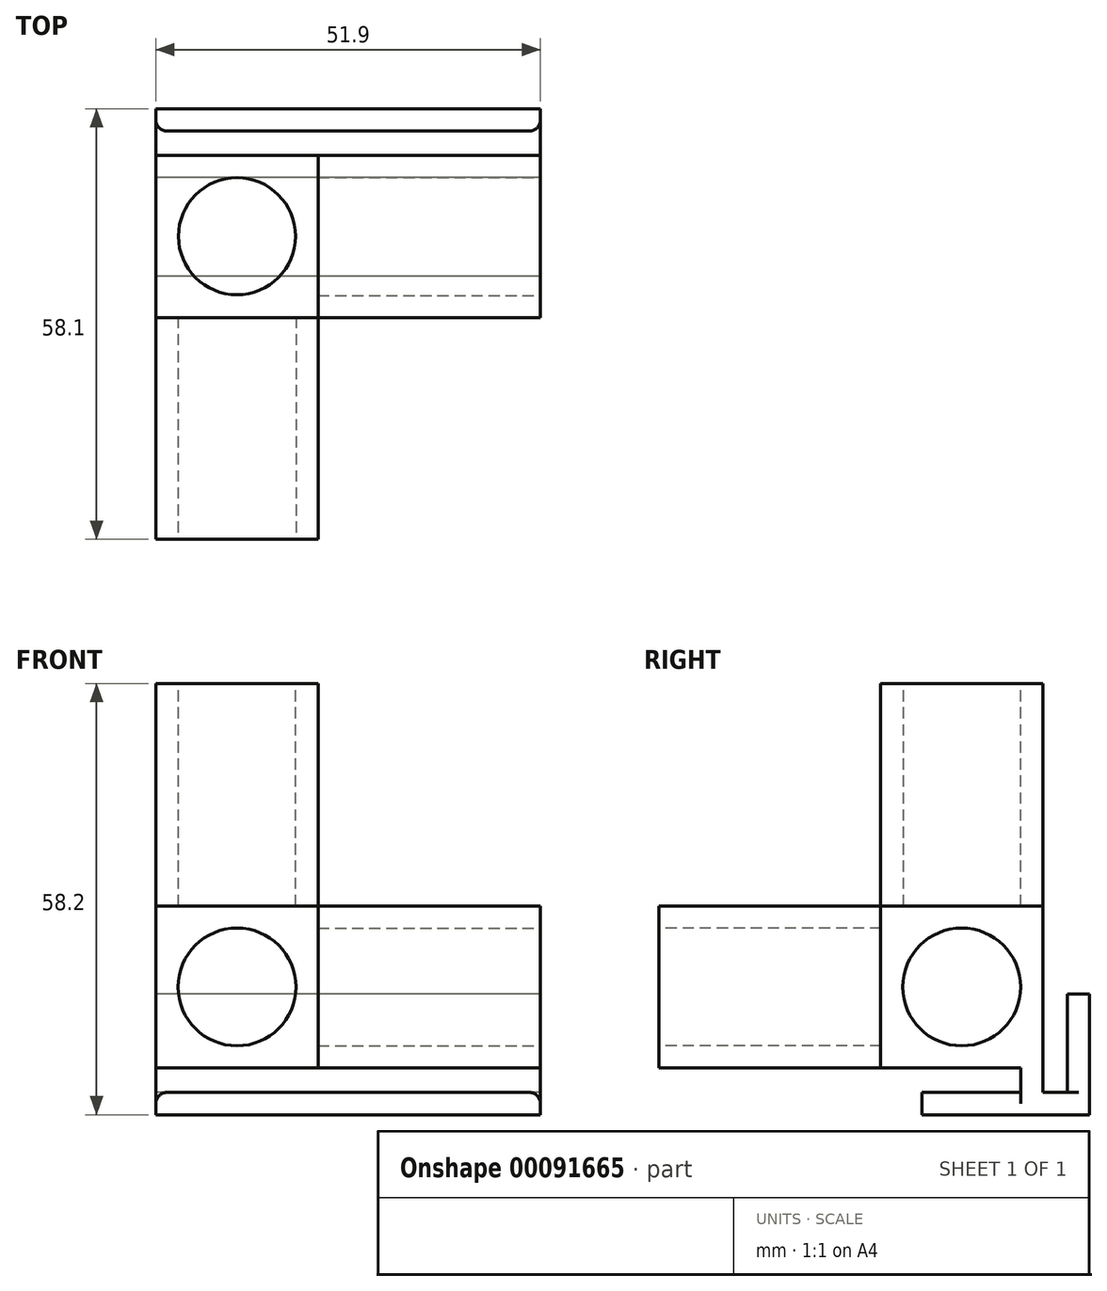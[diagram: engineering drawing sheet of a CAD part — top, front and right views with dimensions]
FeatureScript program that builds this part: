
annotation { "Feature Type Name" : "Feature", "Feature Type Description" : "" }
export const myFeature = defineFeature(function(context is Context, id is Id, definition is map)
    precondition{}
    {
        {
            var Q0;
            Q0=qCreatedBy(makeId("Front.planeOp"),FACE);
            var sketch = newSketch(context, id + "F0", { "sketchPlane" : qUnion([Q0])});
            skLineSegment(sketch, "E0.bottom", {"start": v(-42.3, 45.9) * mm, "end": v(-26.4, 45.9) * mm});
            skLineSegment(sketch, "E0.top", {"start": v(-42.3, 0) * mm, "end": v(-26.4, 0) * mm});
            skLineSegment(sketch, "E0.left", {"start": v(-42.3, 45.9) * mm, "end": v(-42.3, 0) * mm});
            skLineSegment(sketch, "E0.right", {"start": v(-26.4, 45.9) * mm, "end": v(-26.4, 15.9) * mm});
            skLineSegment(sketch, "E1.top", {"start": v(-42.3, 15.9) * mm, "end": v(-26.4, 15.9) * mm});
            skLineSegment(sketch, "E1.left", {"start": v(-42.3, 0) * mm, "end": v(-42.3, 15.9) * mm});
            skLineSegment(sketch, "E1.right", {"start": v(3.6, 0) * mm, "end": v(3.6, 15.9) * mm});
            skLineSegment(sketch, "E2", {"start": v(-26.4, 15.9) * mm, "end": v(-26.4, 0) * mm});
            skLineSegment(sketch, "E3", {"start": v(-26.4, 15.9) * mm, "end": v(3.6, 15.9) * mm});
            skLineSegment(sketch, "E4", {"start": v(-26.4, 0) * mm, "end": v(-26.4, 0) * mm});
            skLineSegment(sketch, "E5", {"start": v(-42.3, 15.9) * mm, "end": v(-42.3, 15.9) * mm});
            skLineSegment(sketch, "E6", {"start": v(-26.4, 0) * mm, "end": v(3.6, 0) * mm});
            skLineSegment(sketch, "E7.0", {"start": v(-45.3, 48.9) * mm, "end": v(-45.3, -3) * mm});
            skLineSegment(sketch, "E7.1", {"start": v(-45.3, -3) * mm, "end": v(-23.4, -3) * mm});
            skLineSegment(sketch, "E7.2", {"start": v(-23.4, 48.9) * mm, "end": v(-23.4, 18.9) * mm});
            skLineSegment(sketch, "E7.3", {"start": v(-23.4, 18.9) * mm, "end": v(6.6, 18.9) * mm});
            skLineSegment(sketch, "E7.4", {"start": v(6.6, -3) * mm, "end": v(6.6, 18.9) * mm});
            skLineSegment(sketch, "E7.5", {"start": v(-45.3, 48.9) * mm, "end": v(-23.4, 48.9) * mm});
            skLineSegment(sketch, "E7.6", {"start": v(-23.4, -3) * mm, "end": v(6.6, -3) * mm});
            skPoint(sketch, "E8", {"position": v(-34.36, 7.95) * mm});
            skPoint(sketch, "E8.positionSnap0", {"position": v(-26.4, 7.95) * mm});
            skPoint(sketch, "E8.positionSnap1", {"position": v(-34.36, 15.9) * mm});
            skCircle(sketch, "E9", {"center": v(-34.36, 7.95) * mm, "radius": 7.95 * mm});
            skLineSegment(sketch, "E10", {"start": v(-23.4, 18.9) * mm, "end": v(-45.3, 18.9) * mm});
            skLineSegment(sketch, "E11", {"start": v(-23.4, 18.9) * mm, "end": v(-23.4, -3) * mm});
            skSolve(sketch);
        }
        {
            var Q0;
            {var subQ1=sQuery(id+"F0.wireOp",EDGE,"E1.top");var subQ3=sQuery(id+"F0.wireOp",EDGE,"E9");var subQ4=makeQuery(id+"F0.imprint","INTERSECT",VERTEX,{"derivedFrom":[subQ1,subQ3]});Q0=makeQuery(id+"F0.imprint","IMPRINT",FACE,{"disambiguationData":[TD([[makeQuery(id+"F0.imprint","IMPRINT",EDGE,{"disambiguationData":[TD([[subQ4,-1.0]])],"derivedFrom":subQ3}),-1.0]])]});}
            var Q1;
            {var subQ0=sQuery(id+"F0.wireOp",EDGE,"E9");var subQ1=makeQuery(id+"F0.imprint","INTERSECT",VERTEX,{"derivedFrom":[sQuery(id+"F0.wireOp",EDGE,"E1.top"),subQ0]});Q1=makeQuery(id+"F0.imprint","IMPRINT",FACE,{"disambiguationData":[TD([[makeQuery(id+"F0.imprint","IMPRINT",EDGE,{"disambiguationData":[TD([[subQ1,1.0]])],"derivedFrom":subQ0}),1.0]])]});}
            var Q2;
            {var subQ5=sQuery(id+"F0.wireOp",EDGE,"E0.bottom");Q2=makeQuery(id+"F0.imprint","IMPRINT",FACE,{"disambiguationData":[TD([[makeQuery(id+"F0.imprint","IMPRINT",EDGE,{"derivedFrom":subQ5}),1.0]])]});}
            var Q3;
            {var subQ0=sQuery(id+"F0.wireOp",EDGE,"E1.right");Q3=makeQuery(id+"F0.imprint","IMPRINT",FACE,{"disambiguationData":[TD([[makeQuery(id+"F0.imprint","IMPRINT",EDGE,{"derivedFrom":subQ0}),1.0]])]});}
            var Q4;
            {var subQ0=sQuery(id+"F0.wireOp",EDGE,"E0.bottom");Q4=makeQuery(id+"F0.imprint","IMPRINT",FACE,{"disambiguationData":[TD([[makeQuery(id+"F0.imprint","IMPRINT",EDGE,{"derivedFrom":subQ0}),-1.0]])]});}
            var Q5;
            {var subQ0=sQuery(id+"F0.wireOp",EDGE,"E1.left");var subQ1=sQuery(id+"F0.wireOp",EDGE,"E0.top");var subQ2=makeQuery(id+"F0.imprint","INTERSECT",VERTEX,{"derivedFrom":[subQ1,subQ0]});Q5=makeQuery(id+"F0.imprint","IMPRINT",FACE,{"disambiguationData":[TD([[makeQuery(id+"F0.imprint","IMPRINT",EDGE,{"disambiguationData":[TD([[subQ2,-1.0]])],"derivedFrom":subQ1}),1.0]])]});}
            var Q6;
            {var subQ1=sQuery(id+"F0.wireOp",EDGE,"E0.top");var subQ3=sQuery(id+"F0.wireOp",EDGE,"E9");var subQ4=makeQuery(id+"F0.imprint","INTERSECT",VERTEX,{"derivedFrom":[subQ1,subQ3]});Q6=makeQuery(id+"F0.imprint","IMPRINT",FACE,{"disambiguationData":[TD([[makeQuery(id+"F0.imprint","IMPRINT",EDGE,{"disambiguationData":[TD([[subQ4,-1.0]])],"derivedFrom":subQ3}),-1.0]])]});}
            var Q7;
            {var subQ1=sQuery(id+"F0.wireOp",EDGE,"E1.top");var subQ3=sQuery(id+"F0.wireOp",EDGE,"E9");var subQ4=makeQuery(id+"F0.imprint","INTERSECT",VERTEX,{"derivedFrom":[subQ1,subQ3]});Q7=makeQuery(id+"F0.imprint","IMPRINT",FACE,{"disambiguationData":[TD([[makeQuery(id+"F0.imprint","IMPRINT",EDGE,{"disambiguationData":[TD([[subQ4,1.0]])],"derivedFrom":subQ3}),-1.0]])]});}
            var Q8;
            {var subQ5=sQuery(id+"F0.wireOp",EDGE,"E1.right");Q8=makeQuery(id+"F0.imprint","IMPRINT",FACE,{"disambiguationData":[TD([[makeQuery(id+"F0.imprint","IMPRINT",EDGE,{"derivedFrom":subQ5}),-1.0]])]});}
            var Q9;
            {var subQ4=sQuery(id+"F0.wireOp",EDGE,"E0.left");var subQ6=sQuery(id+"F0.wireOp",EDGE,"E10");var subQ8=makeQuery(id+"F0.imprint","INTERSECT",VERTEX,{"derivedFrom":[subQ4,subQ6]});Q9=makeQuery(id+"F0.imprint","IMPRINT",FACE,{"disambiguationData":[TD([[makeQuery(id+"F0.imprint","IMPRINT",EDGE,{"disambiguationData":[TD([[subQ8,1.0]])],"derivedFrom":subQ6}),1.0]])]});}
            var Q10;
            {var subQ3=sQuery(id+"F0.wireOp",EDGE,"E11");var subQ5=sQuery(id+"F0.wireOp",EDGE,"E3");var subQ8=makeQuery(id+"F0.imprint","INTERSECT",VERTEX,{"derivedFrom":[subQ5,subQ3]});Q10=makeQuery(id+"F0.imprint","IMPRINT",FACE,{"disambiguationData":[TD([[makeQuery(id+"F0.imprint","IMPRINT",EDGE,{"disambiguationData":[TD([[subQ8,-1.0]])],"derivedFrom":subQ3}),-1.0]])]});}
            var Q11;
            {var subQ14=sQuery(id+"F0.wireOp",EDGE,"E7.1");Q11=makeQuery(id+"F0.imprint","IMPRINT",FACE,{"disambiguationData":[TD([[makeQuery(id+"F0.imprint","IMPRINT",EDGE,{"derivedFrom":subQ14}),1.0]])]});}
            var Q12;
            {var subQ1=sQuery(id+"F0.wireOp",EDGE,"E0.right");var subQ3=sQuery(id+"F0.wireOp",EDGE,"E10");var subQ4=makeQuery(id+"F0.imprint","INTERSECT",VERTEX,{"derivedFrom":[subQ1,subQ3]});Q12=makeQuery(id+"F0.imprint","IMPRINT",FACE,{"disambiguationData":[TD([[makeQuery(id+"F0.imprint","IMPRINT",EDGE,{"disambiguationData":[TD([[subQ4,-1.0]])],"derivedFrom":subQ1}),1.0]])]});}
            extrude(context, id + "F1", {"entities" : qUnion([Q0, Q1, Q2, Q3, Q4, Q5, Q6, Q7, Q8, Q9, Q10, Q11, Q12]), "depth" : (15.9 + 6) * mm});
        }
        {
            var Q0;
            {var subQ14=sQuery(id+"F0.wireOp",EDGE,"E7.1");Q0=makeQuery(id+"F0.imprint","IMPRINT",FACE,{"disambiguationData":[TD([[makeQuery(id+"F0.imprint","IMPRINT",EDGE,{"derivedFrom":subQ14}),1.0]])]});}
            var Q1;
            {var subQ0=sQuery(id+"F0.wireOp",EDGE,"E9");var subQ1=makeQuery(id+"F0.imprint","INTERSECT",VERTEX,{"derivedFrom":[sQuery(id+"F0.wireOp",EDGE,"E1.top"),subQ0]});Q1=makeQuery(id+"F0.imprint","IMPRINT",FACE,{"disambiguationData":[TD([[makeQuery(id+"F0.imprint","IMPRINT",EDGE,{"disambiguationData":[TD([[subQ1,1.0]])],"derivedFrom":subQ0}),1.0]])]});}
            var Q2;
            {var subQ4=sQuery(id+"F0.wireOp",EDGE,"E0.left");var subQ6=sQuery(id+"F0.wireOp",EDGE,"E10");var subQ8=makeQuery(id+"F0.imprint","INTERSECT",VERTEX,{"derivedFrom":[subQ4,subQ6]});Q2=makeQuery(id+"F0.imprint","IMPRINT",FACE,{"disambiguationData":[TD([[makeQuery(id+"F0.imprint","IMPRINT",EDGE,{"disambiguationData":[TD([[subQ8,1.0]])],"derivedFrom":subQ6}),1.0]])]});}
            var Q3;
            {var subQ3=sQuery(id+"F0.wireOp",EDGE,"E11");var subQ5=sQuery(id+"F0.wireOp",EDGE,"E3");var subQ8=makeQuery(id+"F0.imprint","INTERSECT",VERTEX,{"derivedFrom":[subQ5,subQ3]});Q3=makeQuery(id+"F0.imprint","IMPRINT",FACE,{"disambiguationData":[TD([[makeQuery(id+"F0.imprint","IMPRINT",EDGE,{"disambiguationData":[TD([[subQ8,-1.0]])],"derivedFrom":subQ3}),-1.0]])]});}
            var Q4;
            {var subQ1=sQuery(id+"F0.wireOp",EDGE,"E0.right");var subQ3=sQuery(id+"F0.wireOp",EDGE,"E10");var subQ4=makeQuery(id+"F0.imprint","INTERSECT",VERTEX,{"derivedFrom":[subQ1,subQ3]});Q4=makeQuery(id+"F0.imprint","IMPRINT",FACE,{"disambiguationData":[TD([[makeQuery(id+"F0.imprint","IMPRINT",EDGE,{"disambiguationData":[TD([[subQ4,-1.0]])],"derivedFrom":subQ1}),1.0]])]});}
            var Q5;
            {var subQ1=sQuery(id+"F0.wireOp",EDGE,"E1.top");var subQ3=sQuery(id+"F0.wireOp",EDGE,"E9");var subQ4=makeQuery(id+"F0.imprint","INTERSECT",VERTEX,{"derivedFrom":[subQ1,subQ3]});Q5=makeQuery(id+"F0.imprint","IMPRINT",FACE,{"disambiguationData":[TD([[makeQuery(id+"F0.imprint","IMPRINT",EDGE,{"disambiguationData":[TD([[subQ4,1.0]])],"derivedFrom":subQ3}),-1.0]])]});}
            var Q6;
            {var subQ1=sQuery(id+"F0.wireOp",EDGE,"E1.top");var subQ3=sQuery(id+"F0.wireOp",EDGE,"E9");var subQ4=makeQuery(id+"F0.imprint","INTERSECT",VERTEX,{"derivedFrom":[subQ1,subQ3]});Q6=makeQuery(id+"F0.imprint","IMPRINT",FACE,{"disambiguationData":[TD([[makeQuery(id+"F0.imprint","IMPRINT",EDGE,{"disambiguationData":[TD([[subQ4,-1.0]])],"derivedFrom":subQ3}),-1.0]])]});}
            var Q7;
            {var subQ0=sQuery(id+"F0.wireOp",EDGE,"E1.left");var subQ1=sQuery(id+"F0.wireOp",EDGE,"E0.top");var subQ2=makeQuery(id+"F0.imprint","INTERSECT",VERTEX,{"derivedFrom":[subQ1,subQ0]});Q7=makeQuery(id+"F0.imprint","IMPRINT",FACE,{"disambiguationData":[TD([[makeQuery(id+"F0.imprint","IMPRINT",EDGE,{"disambiguationData":[TD([[subQ2,-1.0]])],"derivedFrom":subQ1}),1.0]])]});}
            var Q8;
            {var subQ1=sQuery(id+"F0.wireOp",EDGE,"E0.top");var subQ3=sQuery(id+"F0.wireOp",EDGE,"E9");var subQ4=makeQuery(id+"F0.imprint","INTERSECT",VERTEX,{"derivedFrom":[subQ1,subQ3]});Q8=makeQuery(id+"F0.imprint","IMPRINT",FACE,{"disambiguationData":[TD([[makeQuery(id+"F0.imprint","IMPRINT",EDGE,{"disambiguationData":[TD([[subQ4,-1.0]])],"derivedFrom":subQ3}),-1.0]])]});}
            extrude(context, id + "F2", {"entities" : qUnion([Q0, Q1, Q2, Q3, Q4, Q5, Q6, Q7, Q8]), "operationType" : NewBodyOperationType.ADD, "depth" : (15.8 + 6 + 30) * mm});
        }
        {
            var Q0;
            Q0=makeQuery(id+"F2.opExtrude","CAP_FACE",FACE,{"disambiguationData":[OSD([sQuery(id+"F0.wireOp",EDGE,"E7.0"),sQuery(id+"F0.wireOp",EDGE,"E7.1"),sQuery(id+"F0.wireOp",EDGE,"E10"),sQuery(id+"F0.wireOp",EDGE,"E11")])],"isStart":false});
            var sketch = newSketch(context, id + "F3", { "sketchPlane" : qUnion([Q0])});
            skCircle(sketch, "E12.0", {"center": v(-34.36, 7.95) * mm, "radius": 7.95 * mm});
            skSolve(sketch);
        }
        {
            var Q0;
            Q0=makeQuery(id+"F1.opExtrude","SWEPT_FACE",FACE,{"disambiguationData":[OSD([sQuery(id+"F0.wireOp",EDGE,"E7.5")])]});
            var sketch = newSketch(context, id + "F4", { "sketchPlane" : qUnion([Q0])});
            skPoint(sketch, "E13", {"position": v(-34.36, -3) * mm});
            skPoint(sketch, "E14", {"position": v(-26.4, -10.9) * mm});
            skPoint(sketch, "E15", {"position": v(-34.36, -10.9) * mm});
            skPoint(sketch, "E16", {"position": v(-62.98, 75) * mm});
            skPoint(sketch, "E17.orphan", {"position": v(-42.3, -3) * mm});
            skPoint(sketch, "E18.orphan", {"position": v(-26.4, -3) * mm});
            skPoint(sketch, "E19.orphan", {"position": v(-26.4, -18.8) * mm});
            skCircle(sketch, "E20", {"center": v(-34.36, -10.9) * mm, "radius": 7.9 * mm});
            skSolve(sketch);
        }
        {
            var Q0;
            Q0=makeQuery(id+"F1.opExtrude","SWEPT_FACE",FACE,{"disambiguationData":[OSD([sQuery(id+"F0.wireOp",EDGE,"E7.4")])]});
            var sketch = newSketch(context, id + "F5", { "sketchPlane" : qUnion([Q0])});
            skLineSegment(sketch, "E21.0", {"start": v(-18.9, 15.9) * mm, "end": v(-3, 15.9) * mm});
            skLineSegment(sketch, "E21.1", {"start": v(-18.9, 0) * mm, "end": v(-18.9, 15.9) * mm});
            skLineSegment(sketch, "E21.2", {"start": v(-18.9, 0) * mm, "end": v(-3, 0) * mm});
            skLineSegment(sketch, "E21.3", {"start": v(-3, 0) * mm, "end": v(-3, 15.9) * mm});
            skCircle(sketch, "E22", {"center": v(-10.95, 7.95) * mm, "radius": 7.95 * mm});
            skPoint(sketch, "E22.centerSnap0", {"position": v(-10.95, 0) * mm});
            skPoint(sketch, "E22.centerSnap1", {"position": v(-3, 7.95) * mm});
            skSolve(sketch);
        }
        {
            var Q0;
            Q0=makeQuery(id+"F3.imprint","IMPRINT",FACE,{"disambiguationData":[TD([[makeQuery(id+"F3.imprint","IMPRINT",EDGE,{"derivedFrom":sQuery(id+"F3.wireOp",EDGE,"E12.0")}),1.0]])]});
            extrude(context, id + "F6", {"entities" : qUnion([Q0]), "operationType" : NewBodyOperationType.REMOVE, "oppositeDirection" : true, "depth" : 30 * mm});
        }
        {
            var Q0;
            {var subQ0=sQuery(id+"F5.wireOp",EDGE,"E22");var subQ1=makeQuery(id+"F5.imprint","INTERSECT",VERTEX,{"derivedFrom":[sQuery(id+"F5.wireOp",EDGE,"E21.1"),subQ0]});Q0=makeQuery(id+"F5.imprint","IMPRINT",FACE,{"disambiguationData":[TD([[makeQuery(id+"F5.imprint","IMPRINT",EDGE,{"disambiguationData":[TD([[subQ1,1.0]])],"derivedFrom":subQ0}),1.0]])]});}
            extrude(context, id + "F7", {"entities" : qUnion([Q0]), "operationType" : NewBodyOperationType.REMOVE, "oppositeDirection" : true, "depth" : 30 * mm});
        }
        {
            var Q0;
            Q0=makeQuery(id+"F4.imprint","IMPRINT",FACE,{"disambiguationData":[TD([[makeQuery(id+"F4.imprint","IMPRINT",EDGE,{"derivedFrom":sQuery(id+"F4.wireOp",EDGE,"E20")}),1.0]])]});
            var Q1;
            Q1=sQuery(id+"F4.wireOp",EDGE,"E20");
            extrude(context, id + "F8", {"entities" : qUnion([Q0]), "operationType" : NewBodyOperationType.REMOVE, "surfaceEntities" : qUnion([Q1]), "oppositeDirection" : true, "depth" : 30 * mm});
        }
        {
            var Q0;
            {var subQ0=sQuery(id+"F0.wireOp",EDGE,"E7.0");Q0=makeQuery(id+"F2.boolean.opBoolean","MERGE",FACE,{"derivedFrom":[makeQuery(id+"F1.opExtrude","SWEPT_FACE",FACE,{"disambiguationData":[OSD([subQ0])]}),makeQuery(id+"F2.opExtrude","SWEPT_FACE",FACE,{"disambiguationData":[OSD([subQ0])]})]});}
            var sketch = newSketch(context, id + "F9", { "sketchPlane" : qUnion([Q0])});
            skLineSegment(sketch, "E23.0.0", {"start": v(0, -3) * mm, "end": v(51.8, -3) * mm});
            skLineSegment(sketch, "E23.0.2", {"start": v(51.8, 18.9) * mm, "end": v(21.9, 18.9) * mm});
            skLineSegment(sketch, "E23.0.4", {"start": v(21.9, 48.9) * mm, "end": v(0, 48.9) * mm});
            skLineSegment(sketch, "E24", {"start": v(0, -3) * mm, "end": v(0, -9.3) * mm});
            skLineSegment(sketch, "E25", {"start": v(0, -9.3) * mm, "end": v(16.3, -9.3) * mm});
            skLineSegment(sketch, "E26", {"start": v(16.3, -9.3) * mm, "end": v(16.3, -6.3) * mm});
            skLineSegment(sketch, "E27", {"start": v(16.3, -6.3) * mm, "end": v(3, -6.3) * mm});
            skLineSegment(sketch, "E28", {"start": v(3, -6.3) * mm, "end": v(3, -3) * mm});
            skLineSegment(sketch, "E29", {"start": v(0, -9.3) * mm, "end": v(-3.3, -9.3) * mm});
            skLineSegment(sketch, "E30", {"start": v(-3.3, -9.3) * mm, "end": v(-3.3, -6.3) * mm});
            skLineSegment(sketch, "E31", {"start": v(-3.3, -6.3) * mm, "end": v(0, -6.3) * mm});
            skLineSegment(sketch, "E32", {"start": v(-3.3, -9.3) * mm, "end": v(-6.3, -9.3) * mm});
            skLineSegment(sketch, "E33", {"start": v(-6.3, -9.3) * mm, "end": v(-6.3, 7) * mm});
            skLineSegment(sketch, "E34", {"start": v(-6.3, 7) * mm, "end": v(-3.3, 7) * mm});
            skLineSegment(sketch, "E35", {"start": v(-3.3, 7) * mm, "end": v(-3.3, -6.3) * mm});
            skSolve(sketch);
        }
        {
            var Q0;
            {var subQ0=sQuery(id+"F9.wireOp",EDGE,"E25");Q0=makeQuery(id+"F9.imprint","IMPRINT",FACE,{"disambiguationData":[TD([[makeQuery(id+"F9.imprint","IMPRINT",EDGE,{"derivedFrom":subQ0}),1.0]])]});}
            var Q1;
            {var subQ0=sQuery(id+"F9.wireOp",EDGE,"E29");Q1=makeQuery(id+"F9.imprint","IMPRINT",FACE,{"disambiguationData":[TD([[makeQuery(id+"F9.imprint","IMPRINT",EDGE,{"derivedFrom":subQ0}),-1.0]])]});}
            var Q2;
            Q2=makeQuery(id+"F9.imprint","IMPRINT",FACE,{"disambiguationData":[TD([[makeQuery(id+"F9.imprint","IMPRINT",EDGE,{"derivedFrom":sQuery(id+"F9.wireOp",EDGE,"E30")}),1.0]])]});
            extrude(context, id + "F10", {"entities" : qUnion([Q0, Q1, Q2]), "operationType" : NewBodyOperationType.ADD, "oppositeDirection" : true, "depth" : (6 + 15.9 + 30) * mm});
        }
        {
            var Q0;
            Q0=makeQuery(id+"F10.opExtrude","CAP_EDGE",EDGE,{"disambiguationData":[OSD([sQuery(id+"F9.wireOp",EDGE,"E27")])],"isStart":true});
            var Q1;
            Q1=makeQuery(id+"F10.opExtrude","CAP_EDGE",EDGE,{"disambiguationData":[OSD([sQuery(id+"F9.wireOp",EDGE,"E27")])],"isStart":false});
            var Q2;
            Q2=makeQuery(id+"F10.opExtrude","CAP_EDGE",EDGE,{"disambiguationData":[OSD([sQuery(id+"F9.wireOp",EDGE,"E35")])],"isStart":true});
            var Q3;
            Q3=makeQuery(id+"F10.opExtrude","CAP_EDGE",EDGE,{"disambiguationData":[OSD([sQuery(id+"F9.wireOp",EDGE,"E35")])],"isStart":false});
            fillet(context, id + "F11", {"entities" : qUnion([Q0, Q1, Q2, Q3]), "radius" : 1.5 * mm, "tangentPropagation" : true, "allowEdgeOverflow" : false});
        }
    });
